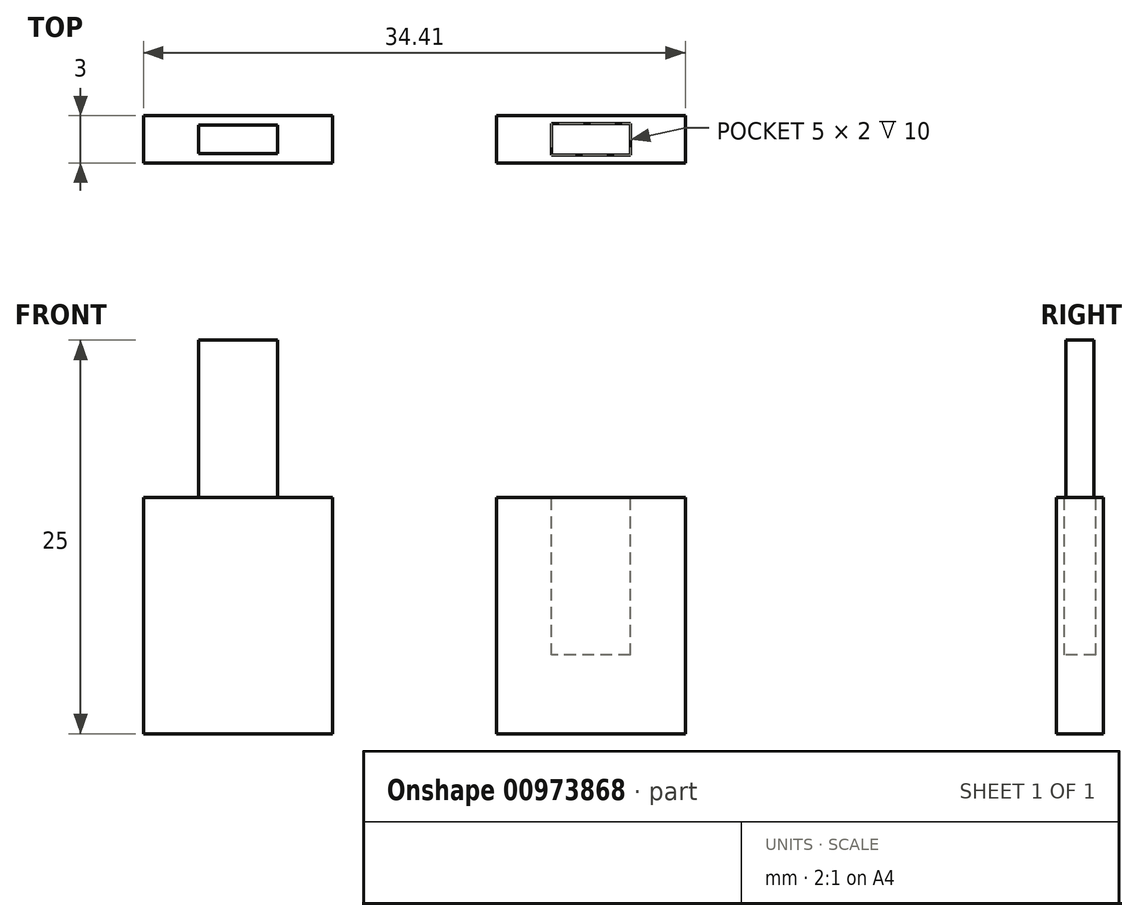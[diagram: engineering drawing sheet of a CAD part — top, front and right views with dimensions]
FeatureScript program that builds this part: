
annotation { "Feature Type Name" : "Feature", "Feature Type Description" : "" }
export const myFeature = defineFeature(function(context is Context, id is Id, definition is map)
    precondition{}
    {
        {
            var Q0;
            Q0=qCreatedBy(makeId("Top.planeOp"),FACE);
            var sketch = newSketch(context, id + "F0", { "sketchPlane" : qUnion([Q0])});
            skLineSegment(sketch, "E0.bottom", {"start": v(-12.48, 10.52) * mm, "end": v(-24.48, 10.52) * mm});
            skLineSegment(sketch, "E0.top", {"start": v(-12.48, 7.52) * mm, "end": v(-24.48, 7.52) * mm});
            skLineSegment(sketch, "E0.left", {"start": v(-12.48, 10.52) * mm, "end": v(-12.48, 7.52) * mm});
            skLineSegment(sketch, "E0.right", {"start": v(-24.48, 10.52) * mm, "end": v(-24.48, 7.52) * mm});
            skLineSegment(sketch, "E1.bottom", {"start": v(9.93, 10.52) * mm, "end": v(-2.07, 10.52) * mm});
            skLineSegment(sketch, "E1.top", {"start": v(9.93, 7.52) * mm, "end": v(-2.07, 7.52) * mm});
            skLineSegment(sketch, "E1.left", {"start": v(9.93, 10.52) * mm, "end": v(9.93, 7.52) * mm});
            skLineSegment(sketch, "E1.right", {"start": v(-2.07, 10.52) * mm, "end": v(-2.07, 7.52) * mm});
            skSolve(sketch);
        }
        {
            var Q0;
            Q0=makeQuery(id+"F0.imprint","IMPRINT",FACE,{"disambiguationData":[TD([[makeQuery(id+"F0.imprint","IMPRINT",EDGE,{"derivedFrom":sQuery(id+"F0.wireOp",EDGE,"E0.bottom")}),1.0]])]});
            var Q1;
            Q1=makeQuery(id+"F0.imprint","IMPRINT",FACE,{"disambiguationData":[TD([[makeQuery(id+"F0.imprint","IMPRINT",EDGE,{"derivedFrom":sQuery(id+"F0.wireOp",EDGE,"E1.bottom")}),1.0]])]});
            extrude(context, id + "F1", {"entities" : qUnion([Q0, Q1]), "depth" : 15 * mm, "offsetDistance" : 25 * mm});
        }
        {
            var Q0;
            Q0=makeQuery(id+"F1.opExtrude","CAP_FACE",FACE,{"disambiguationData":[OSD([sQuery(id+"F0.wireOp",EDGE,"E0.bottom"),sQuery(id+"F0.wireOp",EDGE,"E0.top"),sQuery(id+"F0.wireOp",EDGE,"E0.left"),sQuery(id+"F0.wireOp",EDGE,"E0.right")])],"isStart":false});
            var sketch = newSketch(context, id + "F2", { "sketchPlane" : qUnion([Q0])});
            skLineSegment(sketch, "E2.bottom", {"start": v(-15.98, 9.92) * mm, "end": v(-20.98, 9.92) * mm});
            skLineSegment(sketch, "E2.top", {"start": v(-15.98, 8.12) * mm, "end": v(-20.98, 8.12) * mm});
            skLineSegment(sketch, "E2.left", {"start": v(-15.98, 9.92) * mm, "end": v(-15.98, 8.12) * mm});
            skLineSegment(sketch, "E2.right", {"start": v(-20.98, 9.92) * mm, "end": v(-20.98, 8.12) * mm});
            skLineSegment(sketch, "E3.bottom", {"start": v(6.53, 10.02) * mm, "end": v(1.33, 10.02) * mm});
            skLineSegment(sketch, "E3.top", {"start": v(6.53, 8.02) * mm, "end": v(1.33, 8.02) * mm});
            skLineSegment(sketch, "E3.left", {"start": v(6.53, 10.02) * mm, "end": v(6.53, 8.02) * mm});
            skLineSegment(sketch, "E3.right", {"start": v(1.33, 10.02) * mm, "end": v(1.33, 8.02) * mm});
            skSolve(sketch);
        }
        {
            var Q0;
            Q0=makeQuery(id+"F2.imprint","IMPRINT",FACE,{"disambiguationData":[TD([[makeQuery(id+"F2.imprint","IMPRINT",EDGE,{"derivedFrom":sQuery(id+"F2.wireOp",EDGE,"E2.bottom")}),1.0]])]});
            extrude(context, id + "F3", {"entities" : qUnion([Q0]), "operationType" : NewBodyOperationType.ADD, "depth" : 10 * mm, "offsetDistance" : 25 * mm});
        }
        {
            var Q0;
            Q0=makeQuery(id+"F1.opExtrude","CAP_FACE",FACE,{"disambiguationData":[OSD([sQuery(id+"F0.wireOp",EDGE,"E1.bottom"),sQuery(id+"F0.wireOp",EDGE,"E1.top"),sQuery(id+"F0.wireOp",EDGE,"E1.left"),sQuery(id+"F0.wireOp",EDGE,"E1.right")])],"isStart":false});
            var sketch = newSketch(context, id + "F4", { "sketchPlane" : qUnion([Q0])});
            skLineSegment(sketch, "E4.bottom", {"start": v(6.43, 10.02) * mm, "end": v(1.43, 10.02) * mm});
            skLineSegment(sketch, "E4.top", {"start": v(6.43, 8.02) * mm, "end": v(1.43, 8.02) * mm});
            skLineSegment(sketch, "E4.left", {"start": v(6.43, 10.02) * mm, "end": v(6.43, 8.02) * mm});
            skLineSegment(sketch, "E4.right", {"start": v(1.43, 10.02) * mm, "end": v(1.43, 8.02) * mm});
            skSolve(sketch);
        }
        {
            var Q0;
            Q0 = qSketchRegion(id + "F4", true);
            extrude(context, id + "F5", {"entities" : qUnion([Q0]), "operationType" : NewBodyOperationType.REMOVE, "oppositeDirection" : true, "depth" : 10 * mm, "offsetDistance" : 25 * mm});
        }
    });
